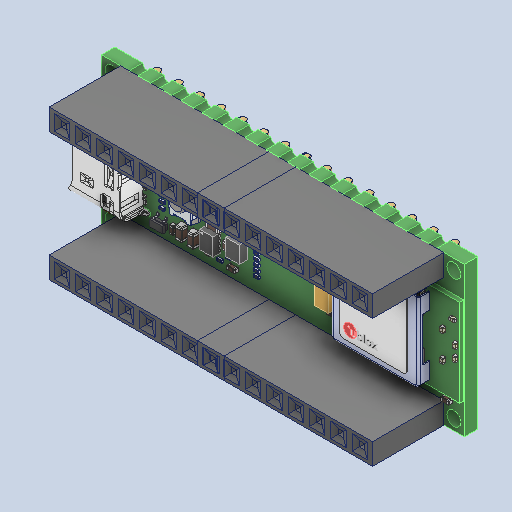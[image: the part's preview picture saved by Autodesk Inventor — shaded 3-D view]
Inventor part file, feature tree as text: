
AUTODESK INVENTOR PART (.ipt)
format: ipt  version: 2024.2 (Build 282272000, 272)  size: 6,375,424 bytes
history: native  units: mm
features: other x408, extrude x90
ambient origin geometry x8: Origin, YZ Plane, XZ Plane, XY Plane, X Axis, Y Axis, Z Axis, Center Point
bodies: Body1 (feature_tree), Body2 (feature_tree), Body3 (feature_tree), Body4 (feature_tree), Body5 (feature_tree), Body6 (feature_tree), Body7 (feature_tree), Body8 (feature_tree), Body9 (feature_tree), Body10 (feature_tree), Body11 (feature_tree), Body12 (feature_tree), Body13 (feature_tree), Body14 (feature_tree), Body15 (feature_tree), Body16 (feature_tree), Body17 (feature_tree), Body18 (feature_tree), Body19 (feature_tree), Body20 (feature_tree), Body21 (feature_tree), Body22 (feature_tree), Body23 (feature_tree), Body24 (feature_tree), Body25 (feature_tree), Body26 (feature_tree), Body27 (feature_tree), Body28 (feature_tree), Body29 (feature_tree), Body30 (feature_tree), Body31 (feature_tree), Body32 (feature_tree), Body33 (feature_tree), Body34 (feature_tree), Body35 (feature_tree), Body36 (feature_tree), Body37 (feature_tree), Body38 (feature_tree), Body39 (feature_tree), Body40 (feature_tree), Body41 (feature_tree), Body42 (feature_tree), Body43 (feature_tree), Body44 (feature_tree), Body45 (feature_tree), Body46 (feature_tree), Body47 (feature_tree), Body48 (feature_tree), Body49 (feature_tree), Body50 (feature_tree), Body51 (feature_tree), Body52 (feature_tree), Body53 (feature_tree), Body54 (feature_tree), Body55 (feature_tree), Body56 (feature_tree), Body57 (feature_tree), Body58 (feature_tree), Body59 (feature_tree), Body60 (feature_tree), Body61 (feature_tree), Body62 (feature_tree), Body63 (feature_tree), Body64 (feature_tree), Body65 (feature_tree), Body66 (feature_tree), Body67 (feature_tree), Body68 (feature_tree), Body69 (feature_tree), Body70 (feature_tree), Body71 (feature_tree), Body72 (feature_tree), Body73 (feature_tree), Body74 (feature_tree), Body75 (feature_tree), Body76 (feature_tree), Body77 (feature_tree), Body78 (feature_tree), Body79 (feature_tree), Body80 (feature_tree), Body81 (feature_tree), Body82 (feature_tree), Body83 (feature_tree), Body84 (feature_tree), Body85 (feature_tree), Body86 (feature_tree), Body87 (feature_tree), Body88 (feature_tree), Body89 (feature_tree), Body90 (feature_tree), Body91 (feature_tree), Body92 (feature_tree), Body93 (feature_tree), Body94 (feature_tree), Body95 (feature_tree), Body96 (feature_tree), Body97 (feature_tree), Body98 (feature_tree), Body99 (feature_tree), Body100 (feature_tree), Body101 (feature_tree), Body102 (feature_tree), Body103 (feature_tree), Body104 (feature_tree), Body105 (feature_tree), Body106 (feature_tree), Body107 (feature_tree), Body108 (feature_tree), Body109 (feature_tree), Body110 (feature_tree), Body111 (feature_tree), Body112 (feature_tree), Body113 (feature_tree), Body114 (feature_tree), Body115 (feature_tree), Body116 (feature_tree), Body117 (feature_tree), Body118 (feature_tree), Body119 (feature_tree), Body120 (feature_tree), Body121 (feature_tree), Body122 (feature_tree), Body123 (feature_tree), Body124 (feature_tree), Body125 (feature_tree), Body126 (feature_tree), Body127 (feature_tree), Body128 (feature_tree), Body129 (feature_tree), Body130 (feature_tree), Body131 (feature_tree), Body132 (feature_tree), Body133 (feature_tree), Body134 (feature_tree), Body135 (feature_tree), Body136 (feature_tree), Body137 (feature_tree), Body138 (feature_tree), Body139 (feature_tree), Body140 (feature_tree), Body141 (feature_tree), Body142 (feature_tree), Body143 (feature_tree), Body144 (feature_tree), Body145 (feature_tree), Body146 (feature_tree), Body147 (feature_tree), Body148 (feature_tree), Body149 (feature_tree), Body150 (feature_tree), Body151 (feature_tree), Body152 (feature_tree), Body153 (feature_tree), Body154 (feature_tree), Body155 (feature_tree), Body156 (feature_tree), Body157 (feature_tree), Body158 (feature_tree), Body159 (feature_tree), Body160 (feature_tree), Body161 (feature_tree), Body162 (feature_tree), Body163 (feature_tree), Body164 (feature_tree), Body165 (feature_tree), Body166 (feature_tree), Body167 (feature_tree), Body168 (feature_tree), Body169 (feature_tree), Body170 (feature_tree), Body171 (feature_tree), Body172 (feature_tree), Body173 (feature_tree), Body174 (feature_tree), Body175 (feature_tree), Body176 (feature_tree), Body177 (feature_tree), Body178 (feature_tree), Body179 (feature_tree), Body180 (feature_tree), Body181 (feature_tree), Body182 (feature_tree), Body183 (feature_tree), Body184 (feature_tree), Body185 (feature_tree), Body186 (feature_tree), Body187 (feature_tree), Body188 (feature_tree), Body189 (feature_tree), Body190 (feature_tree), Body191 (feature_tree), Body192 (feature_tree), Body193 (feature_tree), Body194 (feature_tree), Body195 (feature_tree), Body196 (feature_tree), Body197 (feature_tree), Body198 (feature_tree), Body199 (feature_tree), Body200 (feature_tree), Body201 (feature_tree), Body202 (feature_tree), Body203 (feature_tree), Body204 (feature_tree), Body205 (feature_tree), Body206 (feature_tree), Body207 (feature_tree), Body208 (feature_tree), Body209 (feature_tree), Body210 (feature_tree), Body211 (feature_tree), Body212 (feature_tree), Body213 (feature_tree), Body214 (feature_tree), Body215 (feature_tree), Body216 (feature_tree), Body217 (feature_tree), Body218 (feature_tree), Body219 (feature_tree), Body220 (feature_tree), Body221 (feature_tree), Body222 (feature_tree), Body223 (feature_tree), Body224 (feature_tree), Body225 (feature_tree), Body226 (feature_tree), Body227 (feature_tree), Body228 (feature_tree), Body229 (feature_tree), Body230 (feature_tree), Body231 (feature_tree), Body232 (feature_tree), Body233 (feature_tree), Body234 (feature_tree), Body235 (feature_tree), Body236 (feature_tree), Body237 (feature_tree), Body238 (feature_tree), Body239 (feature_tree), Body240 (feature_tree), Body241 (feature_tree), Body242 (feature_tree), Body243 (feature_tree), Body244 (feature_tree), Body245 (feature_tree), Body246 (feature_tree), Body247 (feature_tree), Body248 (feature_tree), Body249 (feature_tree), Body250 (feature_tree), Body251 (feature_tree), Body252 (feature_tree), Body253 (feature_tree), Body254 (feature_tree), Body255 (feature_tree), Body256 (feature_tree), Body257 (feature_tree), Body258 (feature_tree)
feature tree (498):
  other  "Sólido1"
  other  "Sólido2"
  other  "Sólido3"
  other  "Sólido4"
  other  "Sólido5"
  other  "Sólido6"
  other  "Sólido7"
  other  "Sólido8"
  other  "Sólido9"
  other  "Sólido10"
  other  "Sólido11"
  other  "Sólido12"
  other  "Sólido13"
  other  "Sólido14"
  other  "Sólido15"
  other  "Sólido16"
  other  "Sólido17"
  other  "Sólido18"
  other  "Sólido19"
  other  "Sólido20"
  other  "Sólido21"
  other  "Sólido22"
  other  "Sólido23"
  other  "Sólido24"
  other  "Sólido25"
  other  "Sólido26"
  other  "Sólido27"
  other  "Sólido28"
  other  "Sólido29"
  other  "Sólido30"
  other  "Sólido31"
  other  "Sólido32"
  other  "Sólido33"
  other  "Sólido34"
  other  "Sólido35"
  other  "Sólido36"
  other  "Sólido37"
  other  "Sólido38"
  other  "Sólido39"
  other  "Sólido40"
  other  "Sólido41"
  other  "Sólido42"
  other  "Sólido43"
  other  "Sólido44"
  other  "Sólido45"
  other  "Sólido46"
  other  "Sólido47"
  other  "Sólido48"
  other  "Sólido49"
  other  "Sólido50"
  other  "Sólido51"
  other  "Sólido52"
  other  "Sólido53"
  other  "Sólido54"
  other  "Sólido55"
  other  "Sólido56"
  other  "Sólido57"
  other  "Sólido58"
  other  "Sólido59"
  other  "Sólido60"
  other  "Sólido61"
  other  "Sólido62"
  other  "Sólido63"
  other  "Sólido64"
  other  "Sólido65"
  other  "Sólido66"
  other  "Sólido67"
  other  "Sólido68"
  other  "Sólido69"
  other  "Sólido70"
  other  "Sólido71"
  other  "Sólido72"
  other  "Sólido73"
  other  "Sólido74"
  other  "Sólido75"
  other  "Sólido76"
  other  "Sólido77"
  other  "Sólido78"
  other  "Sólido79"
  other  "Sólido80"
  other  "Sólido81"
  other  "Sólido82"
  other  "Sólido83"
  other  "Sólido84"
  other  "Sólido85"
  other  "Sólido86"
  other  "Sólido87"
  other  "Sólido88"
  other  "Sólido89"
  other  "Sólido90"
  other  "Sólido91"
  other  "Sólido92"
  other  "Sólido93"
  other  "Sólido94"
  other  "Sólido95"
  other  "Sólido96"
  other  "Sólido97"
  other  "Sólido98"
  other  "Sólido99"
  other  "Sólido100"
  other  "Sólido101"
  other  "Sólido102"
  other  "Sólido103"
  other  "Sólido104"
  other  "Sólido105"
  other  "Sólido106"
  other  "Sólido107"
  other  "Sólido108"
  other  "Sólido109"
  other  "Sólido110"
  other  "Sólido111"
  other  "Sólido112"
  other  "Sólido113"
  other  "Sólido114"
  other  "Sólido115"
  other  "Sólido116"
  other  "Sólido117"
  other  "Sólido118"
  other  "Sólido119"
  other  "Sólido120"
  other  "Sólido121"
  other  "Sólido122"
  other  "Sólido123"
  other  "Sólido124"
  other  "Sólido125"
  other  "Sólido126"
  other  "Sólido127"
  other  "Sólido128"
  other  "Sólido129"
  other  "Sólido130"
  other  "Sólido131"
  other  "Sólido132"
  other  "Sólido133"
  other  "Sólido134"
  other  "Sólido135"
  other  "Sólido136"
  other  "Sólido137"
  other  "Sólido138"
  other  "Sólido139"
  other  "Sólido140"
  other  "Sólido141"
  other  "Sólido142"
  other  "Sólido143"
  other  "Sólido144"
  other  "Sólido145"
  other  "Sólido146"
  other  "Sólido147"
  other  "Sólido148"
  other  "Sólido149"
  other  "Sólido150"
  other  "Sólido151"
  other  "Sólido152"
  other  "Sólido153"
  other  "Sólido154"
  other  "Sólido155"
  other  "Sólido156"
  other  "Sólido157"
  other  "Sólido158"
  other  "Sólido159"
  other  "Sólido160"
  other  "Sólido161"
  other  "Sólido162"
  other  "Sólido163"
  other  "Sólido164"
  other  "Sólido165"
  other  "Sólido166"
  other  "Sólido167"
  other  "Sólido168"
  other  "Sólido169"
  other  "Sólido170"
  other  "Sólido171"
  other  "Sólido172"
  other  "Sólido173"
  other  "Sólido174"
  other  "Sólido175"
  other  "Sólido176"
  other  "Sólido177"
  other  "Sólido178"
  other  "Sólido179"
  other  "Sólido180"
  other  "Sólido181"
  other  "Sólido182"
  other  "Sólido183"
  other  "Sólido184"
  other  "Sólido185"
  other  "Sólido186"
  other  "Sólido187"
  other  "Sólido188"
  other  "Sólido189"
  other  "Sólido190"
  other  "Sólido191"
  other  "Sólido192"
  other  "Sólido193"
  other  "Sólido194"
  other  "Sólido195"
  other  "Sólido196"
  other  "Sólido197"
  other  "Sólido198"
  other  "Sólido199"
  other  "Sólido200"
  other  "Sólido201"
  other  "Sólido202"
  other  "Sólido203"
  other  "Sólido204"
  other  "Sólido205"
  other  "Sólido206"
  other  "Sólido207"
  other  "Sólido208"
  other  "Sólido209"
  other  "Sólido210"
  other  "Sólido211"
  other  "Sólido212"
  other  "Sólido213"
  other  "Sólido214"
  other  "Sólido215"
  other  "Sólido216"
  other  "Sólido217"
  other  "Sólido218"
  other  "Sólido219"
  other  "Sólido220"
  other  "Sólido221"
  other  "Sólido222"
  other  "Sólido223"
  other  "Sólido224"
  other  "Sólido225"
  other  "Sólido226"
  other  "Sólido227"
  other  "Sólido228"
  other  "Sólido229"
  other  "Sólido230"
  other  "Sólido231"
  other  "Sólido232"
  other  "Sólido233"
  other  "Sólido234"
  other  "Sólido235"
  other  "Sólido236"
  other  "Sólido237"
  other  "Sólido238"
  other  "Sólido239"
  other  "Sólido240"
  other  "Sólido241"
  other  "Sólido242"
  other  "Sólido243"
  other  "Sólido244"
  other  "Sólido245"
  other  "Sólido246"
  other  "Sólido247"
  other  "Sólido248"
  other  "Open CASCADE STEP translator 7.5 1.1.1_1:1"
  other  "CAP-0402_3:1"
  extrude  "Extruded_5:1"  [1 undecoded]
  other  "CAP-0201_8:1"
  other  "Open CASCADE STEP translator 6.8 1.1.1_10:1"
  extrude  "Extruded_12:1"  [1 undecoded]
  extrude  "Extruded_12:2"  [1 undecoded]
  extrude  "Extruded_15:1"  [1 undecoded]
  extrude  "Extruded_18:1"  [1 undecoded]
  extrude  "Extruded_12:3"  [1 undecoded]
  extrude  "Extruded_12:4"  [1 undecoded]
  extrude  "Extruded_23:1"  [1 undecoded]
  extrude  "Extruded_23:2"  [1 undecoded]
  extrude  "Extruded_26:1"  [1 undecoded]
  other  "body_29:1"
  other  "pins_30:1"
  other  "pins_30:2"
  other  "pins_30:3"
  other  "pins_30:4"
  other  "pins_30:5"
  other  "pins_30:6"
  other  "pins_30:7"
  other  "pins_30:8"
  other  "pins_30:9"
  other  "pins_30:10"
  other  "pins_30:11"
  other  "pins_30:12"
  other  "pins_30:13"
  other  "pins_30:14"
  other  "pins_30:15"
  other  "pins_30:16"
  other  "pins_30:17"
  other  "pins_30:18"
  other  "pins_30:19"
  other  "pins_30:20"
  other  "pins_30:21"
  other  "pins_30:22"
  other  "pins_30:23"
  other  "pins_30:24"
  other  "pins_30:25"
  other  "pins_30:26"
  other  "pins_30:27"
  other  "pins_30:28"
  other  "pins_30:29"
  other  "pins_30:30"
  other  "pins_30:31"
  other  "pins_30:32"
  other  "pins_30:33"
  other  "pins_30:34"
  other  "pins_30:35"
  other  "pins_30:36"
  other  "pins_30:37"
  other  "pins_30:38"
  other  "pins_30:39"
  other  "pins_30:40"
  other  "pins_30:41"
  other  "pins_30:42"
  other  "pins_30:43"
  other  "pins_30:44"
  other  "pins_30:45"
  other  "pins_30:46"
  other  "pins_30:47"
  other  "pins_30:48"
  other  "pins_30:49"
  other  "pins_30:50"
  other  "pins_30:51"
  other  "pins_30:52"
  other  "pins_30:53"
  other  "pins_30:54"
  other  "pins_30:55"
  other  "pins_30:56"
  other  "pins_30:57"
  other  "logo_31:1"
  other  "logo_31:2"
  other  "logo_31:3"
  other  "logo_31:4"
  other  "logo_31:5"
  other  "logo_31:6"
  other  "logo_31:7"
  other  "logo_31:8"
  other  "logo_31:9"
  other  "logo_31:10"
  other  "logo_31:11"
  other  "logo_31:12"
  other  "logo_31:13"
  other  "logo_31:14"
  other  "logo_31:15"
  other  "logo_31:16"
  other  "logo_31:17"
  other  "logo_31:18"
  other  "logo_31:19"
  other  "logo_31:20"
  other  "logo_31:21"
  other  "logo_31:22"
  extrude  "Extruded_34:1"  [1 undecoded]
  extrude  "Extruded_36:1"  [1 undecoded]
  extrude  "Extruded_36:2"  [1 undecoded]
  extrude  "Extruded_34:2"  [1 undecoded]
  extrude  "Extruded_41:1"  [1 undecoded]
  extrude  "Extruded_41:2"  [1 undecoded]
  extrude  "Extruded_34:3"  [1 undecoded]
  extrude  "Extruded_36:3"  [1 undecoded]
  extrude  "Extruded_36:4"  [1 undecoded]
  extrude  "Extruded_15:2"  [1 undecoded]
  extrude  "Extruded_12:5"  [1 undecoded]
  extrude  "Extruded_12:6"  [1 undecoded]
  extrude  "Extruded_12:7"  [1 undecoded]
  extrude  "Extruded_12:8"  [1 undecoded]
  extrude  "Extruded_15:3"  [1 undecoded]
  extrude  "Extruded_15:4"  [1 undecoded]
  extrude  "Extruded_12:9"  [1 undecoded]
  extrude  "Extruded_12:10"  [1 undecoded]
  extrude  "Extruded_61:1"  [1 undecoded]
  extrude  "Extruded_61:2"  [1 undecoded]
  extrude  "Extruded_15:5"  [1 undecoded]
  extrude  "Extruded_15:6"  [1 undecoded]
  extrude  "Extruded_12:11"  [1 undecoded]
  extrude  "Extruded_12:12"  [1 undecoded]
  extrude  "Extruded_12:13"  [1 undecoded]
  extrude  "Extruded_12:14"  [1 undecoded]
  extrude  "Extruded_15:7"  [1 undecoded]
  extrude  "Extruded_12:15"  [1 undecoded]
  extrude  "Extruded_12:16"  [1 undecoded]
  extrude  "Extruded_15:8"  [1 undecoded]
  extrude  "Extruded_15:9"  [1 undecoded]
  extrude  "Extruded_12:17"  [1 undecoded]
  extrude  "Extruded_12:18"  [1 undecoded]
  extrude  "Extruded_12:19"  [1 undecoded]
  extrude  "Extruded_12:20"  [1 undecoded]
  extrude  "Extruded_84:1"  [1 undecoded]
  extrude  "Extruded_15:10"  [1 undecoded]
  extrude  "Extruded_12:21"  [1 undecoded]
  extrude  "Extruded_12:22"  [1 undecoded]
  other  "label_8x8_91:1"
  other  "logo_x_4mm_92:1"
  other  "logo_o_4mm_93:1"
  other  "logo_l_4mm_94:1"
  other  "logo_b_4mm_95:1"
  other  "logo_u_4mm_96:1"
  other  "MAYA_W1_Shield_UBXH04-0000683_99:1"
  extrude  "Extruded_101:1"  [1 undecoded]
  extrude  "Extruded_12:23"  [1 undecoded]
  extrude  "Extruded_12:24"  [1 undecoded]
  extrude  "Extruded_15:11"  [1 undecoded]
  extrude  "Extruded_61:3"  [1 undecoded]
  extrude  "Extruded_61:4"  [1 undecoded]
  extrude  "Extruded_18:2"  [1 undecoded]
  extrude  "Extruded_61:5"  [1 undecoded]
  extrude  "Extruded_61:6"  [1 undecoded]
  extrude  "Extruded_15:12"  [1 undecoded]
  extrude  "Extruded_15:13"  [1 undecoded]
  extrude  "Extruded_12:25"  [1 undecoded]
  extrude  "Extruded_12:26"  [1 undecoded]
  extrude  "Extruded_12:27"  [1 undecoded]
  extrude  "Extruded_12:28"  [1 undecoded]
  extrude  "Extruded_15:14"  [1 undecoded]
  extrude  "Extruded_12:29"  [1 undecoded]
  extrude  "Extruded_12:30"  [1 undecoded]
  extrude  "Extruded_15:15"  [1 undecoded]
  extrude  "Extruded_15:16"  [1 undecoded]
  extrude  "Extruded_61:7"  [1 undecoded]
  extrude  "Extruded_61:8"  [1 undecoded]
  extrude  "Extruded_132:1"  [1 undecoded]
  extrude  "Extruded_134:1"  [1 undecoded]
  extrude  "Extruded_134:2"  [1 undecoded]
  extrude  "Extruded_15:17"  [1 undecoded]
  extrude  "Extruded_12:31"  [1 undecoded]
  extrude  "Extruded_12:32"  [1 undecoded]
  extrude  "Extruded_15:18"  [1 undecoded]
  extrude  "Extruded_12:33"  [1 undecoded]
  extrude  "Extruded_12:34"  [1 undecoded]
  extrude  "Extruded_132:2"  [1 undecoded]
  extrude  "Extruded_134:3"  [1 undecoded]
  extrude  "Extruded_134:4"  [1 undecoded]
  extrude  "Extruded_61:9"  [1 undecoded]
  extrude  "Extruded_61:10"  [1 undecoded]
  extrude  "Extruded_15:19"  [1 undecoded]
  extrude  "Extruded_15:20"  [1 undecoded]
  extrude  "Extruded_12:35"  [1 undecoded]
  extrude  "Extruded_12:36"  [1 undecoded]
  other  "RES-0402_160:1"
  other  "RES-0402_162:1"
  other  "Open CASCADE STEP translator 6.8 13.2.1_165:1"
  other  "Thermal_Shape_167:1"
  other  "Open CASCADE STEP translator 6.8 13.4.1_168:1"
  other  "Open CASCADE STEP translator 6.8 13.4.1_168:2"
  other  "Open CASCADE STEP translator 6.8 13.4.1_168:3"
  other  "Open CASCADE STEP translator 6.8 13.4.1_168:4"
  other  "Open CASCADE STEP translator 6.8 13.4.1_168:5"
  other  "Open CASCADE STEP translator 6.8 13.4.1_168:6"
  other  "Open CASCADE STEP translator 6.8 13.4.1_168:7"
  other  "Open CASCADE STEP translator 6.8 13.4.1_168:8"
  other  "RES-0201_180:1"
  other  "RES-0201_182:1"
  other  "RES-0201_184:1"
  other  "RES-0201_186:1"
  other  "RES-0201_188:1"
  other  "RES-0201_190:1"
  other  "RES-0201_192:1"
  other  "RES-0201_194:1"
  other  "RES-0201_196:1"
  other  "RES-0201_198:1"
  other  "RES-0201_200:1"
  other  "RES-0201_202:1"
  other  "RES-0201_204:1"
  other  "RES-0201_206:1"
  other  "SOT-523_208:1"
  other  "HSMx-190_210:1"
  other  "CAP-0402_212:1"
  other  "CAP-0201_214:1"
  other  "CAP-0201_216:1"
  other  "CAP-0603_218:1"
  other  "CAP-0402_220:1"
  other  "CAP-0402_222:1"
  other  "CAP-0603_224:1"
  other  "Open CASCADE STEP translator 6.8 19.2.1_227:1"
  other  "Open CASCADE STEP translator 6.8 19.3.1_229:1"
  other  "Open CASCADE STEP translator 6.8 19.3.1_229:2"
  other  "Open CASCADE STEP translator 6.8 19.3.1_229:3"
  other  "Open CASCADE STEP translator 6.8 19.3.1_229:4"
  other  "Open CASCADE STEP translator 6.8 19.3.1_229:5"
  other  "Open CASCADE STEP translator 6.8 19.3.1_229:6"
  other  "Open CASCADE STEP translator 6.8 19.3.1_229:7"
  other  "Open CASCADE STEP translator 6.8 19.3.1_229:8"
  extrude  "Extruded_240:1"  [1 undecoded]
  other  "CAP-0201_243:1"
  other  "CAP-0402_245:1"
  other  "CAP-0402_247:1"
  other  "CAP-0603_249:1"
  other  "CAP-0603_251:1"
  other  "CAP-0603_253:1"
  other  "RES-0201_255:1"
  other  "RES-0201_257:1"
  other  "Open CASCADE STEP translator 7.5 15.1.1_259:1"
  other  "lead_261:1"
  other  "lead_262:1"
  other  "RES-0201_266:1"
  other  "RES-0201_268:1"
  other  "SMLP34RGB_270:1"
  other  "HSMx-190_272:1"
  other  "Header _Fem_1X8_274:1"
  other  "Header _Fem_1X8_275:1"
  other  "Header _Fem_1X8_277:1"
  other  "Header _Fem_1X8_278:1"
  other  "PTS820J20KSMTRLFS_280:1"
  other  "CX90B-16P_3D_282:1"
  other  "PRTR5V0U2X_285:1"
  other  "CAP-0805_287:1"
  other  "Composto1"
  other  "Sup1"
note: 90 required parameter values undecoded (feature->parameter linkage not recoverable at this tier; creation-order binding heuristic only, values carry confidence <= 0.55)
